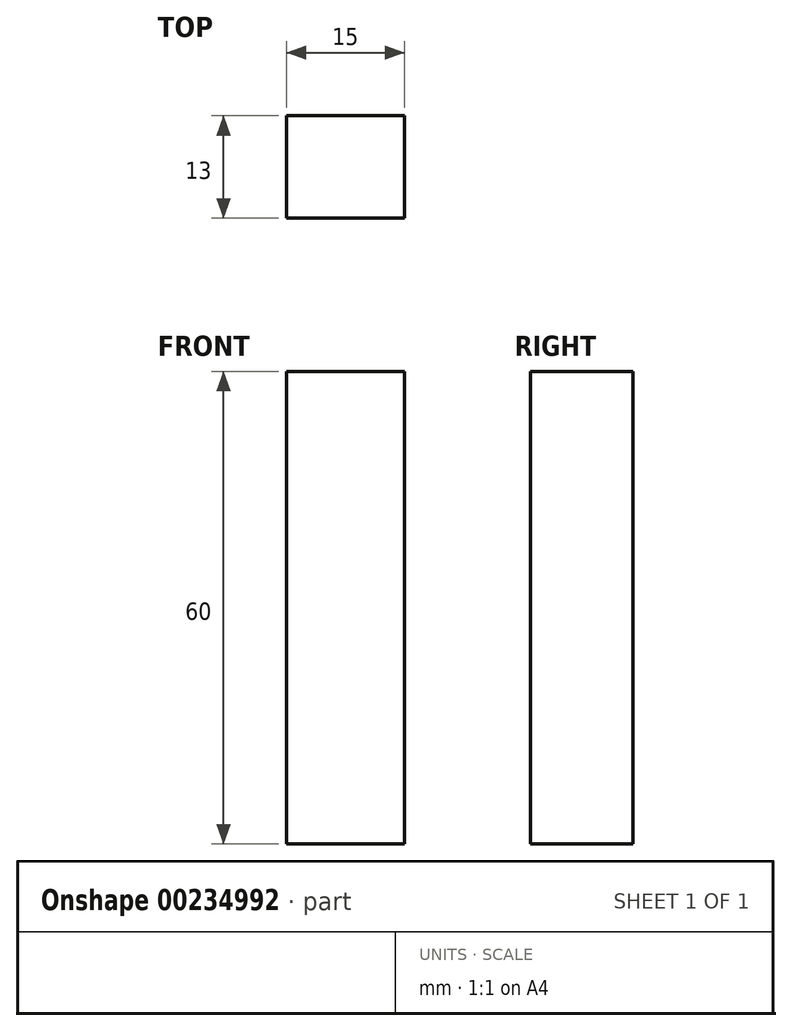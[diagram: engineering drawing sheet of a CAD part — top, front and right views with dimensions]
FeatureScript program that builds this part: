
annotation { "Feature Type Name" : "Feature", "Feature Type Description" : "" }
export const myFeature = defineFeature(function(context is Context, id is Id, definition is map)
    precondition{}
    {
        {
            var Q0;
            Q0=qCreatedBy(makeId("Front.planeOp"),FACE);
            var sketch = newSketch(context, id + "F0", { "sketchPlane" : qUnion([Q0])});
            skLineSegment(sketch, "E0.bottom", {"start": v(7.5, -30) * mm, "end": v(-7.5, -30) * mm});
            skLineSegment(sketch, "E0.top", {"start": v(7.5, 30) * mm, "end": v(-7.5, 30) * mm});
            skLineSegment(sketch, "E0.left", {"start": v(7.5, -30) * mm, "end": v(7.5, 30) * mm});
            skLineSegment(sketch, "E0.right", {"start": v(-7.5, -30) * mm, "end": v(-7.5, 30) * mm});
            skPoint(sketch, "E0.middle", {"position": v(0, 0) * mm});
            skSolve(sketch);
        }
        {
            var Q0;
            Q0 = qSketchRegion(id + "F0", true);
            extrude(context, id + "F1", {"entities" : qUnion([Q0]), "endBound" : BoundingType.SYMMETRIC, "depth" : 13 * mm});
        }
    });
